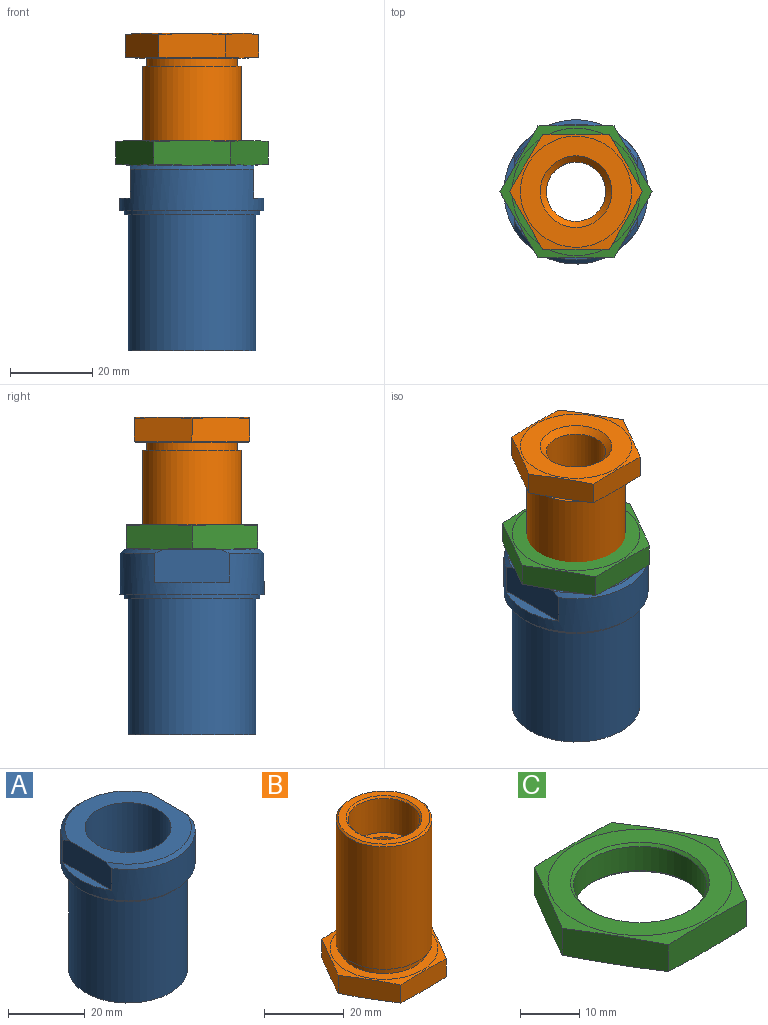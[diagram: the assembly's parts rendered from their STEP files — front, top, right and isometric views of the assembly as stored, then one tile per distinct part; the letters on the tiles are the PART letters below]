
ASSEMBLY  parts=3 mates=4
PART A: 16 faces, bbox 35x35x45 mm
  f0: cylinder r=17.5mm len=35mm, axis (0,0,-1), area 834.4mm2, adj f2,f3,f9,f12,f13,f14,f15
  f1: plane 33x30mm, normal (0,0,1), area 433.5mm2, adj f2,f3,f10,f13,f15
  f2: cone r=17.5mm half-angle=45deg, axis (0,0,-1), area 52mm2, adj f0,f1,f13,f15
  f3: cone r=17.5mm half-angle=45deg, axis (0,0,-1), area 52mm2, adj f0,f1,f13,f15
  f4: cylinder r=13mm len=26mm, axis (0,0,-1), area 816.8mm2, adj f5,f11
  f5: plane 31x31mm, normal (0,0,-1), area 223.8mm2, adj f4,f6
  f6: cylinder r=15.5mm len=33mm, axis (0,0,-1), area 3213.8mm2, adj f5,f7
  f7: plane 33x33mm, normal (0,0,-1), area 100.5mm2, adj f6,f8
  f8: cylinder r=16.5mm len=33mm, axis (0,0,-1), area 103.7mm2, adj f7,f9
  f9: plane 35x35mm, normal (0,0,-1), area 106.8mm2, adj f0,f8
  f10: cylinder r=11.2mm len=35mm, axis (0,0,-1), area 2463mm2, adj f1,f11
  f11: plane 26x26mm, normal (0,0,-1), area 136.8mm2, adj f4,f10
  f12: plane 18.03x2.5mm, normal (0,0,1), area 30.5mm2, adj f0,f13
  f13: plane 18.03x8mm, normal (1,0,0), area 142.2mm2, adj f0,f1,f2,f3,f12
  f14: plane 18.03x2.5mm, normal (0,0,1), area 30.5mm2, adj f0,f15
  f15: plane 18.03x8mm, normal (-1,0,0), area 142.2mm2, adj f0,f1,f2,f3,f14
PART B: 20 faces, bbox 32.3x32.3x46 mm
  f0: plane 27x27mm, normal (0,0,1), area 192.4mm2, adj f3,f10
  f1: plane 27x27mm, normal (0,0,-1), area 334.8mm2, adj f9,f17
  f2: cylinder r=7.2mm len=33.5mm, axis (0,0,1), area 1515.5mm2, adj f7,f17
  f3: cylinder r=11mm len=22mm, axis (0,0,-1), area 138.2mm2, adj f0,f6
  f4: cylinder r=12mm len=37.5mm, axis (0,0,-1), area 2827.4mm2, adj f6,f19
  f5: plane 23x23mm, normal (0,0,1), area 131.9mm2, adj f18,f19
  f6: plane 24x24mm, normal (0,0,-1), area 72.3mm2, adj f3,f4
  f7: plane 18x18mm, normal (0,0,1), area 91.6mm2, adj f2,f8
  f8: cylinder r=9mm len=18mm, axis (0,0,1), area 593.8mm2, adj f7,f18
  f9: cone r=13.5mm half-angle=84.6deg, axis (0,0,1), area 106.9mm2, adj f1,f11,f12,f13,f14,f15,f16
  f10: cone r=13.5mm half-angle=84.6deg, axis (0,0,-1), area 106.9mm2, adj f0,f11,f12,f13,f14,f15,f16
  f11: plane 14x8.08mm, normal (-0.87,-0.5,0), area 93.2mm2, adj f9,f10,f12,f16
  f12: plane 14x8.08mm, normal (-0.87,0.5,0), area 93.2mm2, adj f9,f10,f11,f13
  f13: plane 16.17x5.91mm, normal (0,1,0), area 93.2mm2, adj f9,f10,f12,f14
  f14: plane 14x8.08mm, normal (0.87,0.5,0), area 93.2mm2, adj f9,f10,f13,f15
  f15: plane 14x8.08mm, normal (0.87,-0.5,0), area 93.2mm2, adj f9,f10,f14,f16
  f16: plane 16.17x5.91mm, normal (0,-1,0), area 93.2mm2, adj f9,f10,f11,f15
  f17: cone r=8.7mm half-angle=45deg, axis (0,0,-1), area 106mm2, adj f1,f2
  f18: cone r=9mm half-angle=45deg, axis (0,0,1), area 41.1mm2, adj f5,f8
  f19: cone r=11.5mm half-angle=45deg, axis (0,0,-1), area 52.2mm2, adj f4,f5
PART C: 13 faces, bbox 37x37x6 mm
  f0: plane 31x31mm, normal (0,0,1), area 324.7mm2, adj f3,f11
  f1: plane 31x31mm, normal (0,0,-1), area 324.7mm2, adj f4,f12
  f2: cylinder r=11.2mm len=22.4mm, axis (0,0,-1), area 351.9mm2, adj f11,f12
  f3: cone r=15.5mm half-angle=85.2deg, axis (0,0,-1), area 132.5mm2, adj f0,f5,f6,f7,f8,f9,f10
  f4: cone r=15.5mm half-angle=85.2deg, axis (0,0,1), area 132.5mm2, adj f1,f5,f6,f7,f8,f9,f10
  f5: plane 16x9.24mm, normal (-0.87,-0.5,0), area 106.7mm2, adj f3,f4,f6,f10
  f6: plane 16x9.24mm, normal (-0.87,0.5,0), area 106.7mm2, adj f3,f4,f5,f7
  f7: plane 18.48x5.92mm, normal (0,1,0), area 106.7mm2, adj f3,f4,f6,f8
  f8: plane 16x9.24mm, normal (0.87,0.5,0), area 106.7mm2, adj f3,f4,f7,f9
  f9: plane 16x9.24mm, normal (0.87,-0.5,0), area 106.7mm2, adj f3,f4,f8,f10
  f10: plane 18.48x5.92mm, normal (0,-1,0), area 106.7mm2, adj f3,f4,f5,f9
  f11: cone r=11.2mm half-angle=45deg, axis (0,0,1), area 50.9mm2, adj f0,f2
  f12: cone r=11.7mm half-angle=45deg, axis (0,0,-1), area 50.9mm2, adj f1,f2
PLACE A t=(0.06,-0.1,-22.7)mm fixed
PLACE B rot(axis=(1,0,0),180deg) t=(0.06,-0.1,54.3)mm
PLACE C t=(0.06,-0.1,22.3)mm
MATE planar C.f3 <-> A.f0  axis (0,0,-1) through (0.06,-0.1,22.3)mm
MATE slider B.f2 <-> C.f2  axis (0,0,1) through (0.06,-0.1,27.55)mm
MATE slider C.f2 <-> A.f0  axis (0,0,-1) through (0.06,-0.1,25.3)mm
MATE planar B.f2 <-> C.f3  axis (0,0,-1) through (0.06,-0.1,48.3)mm
